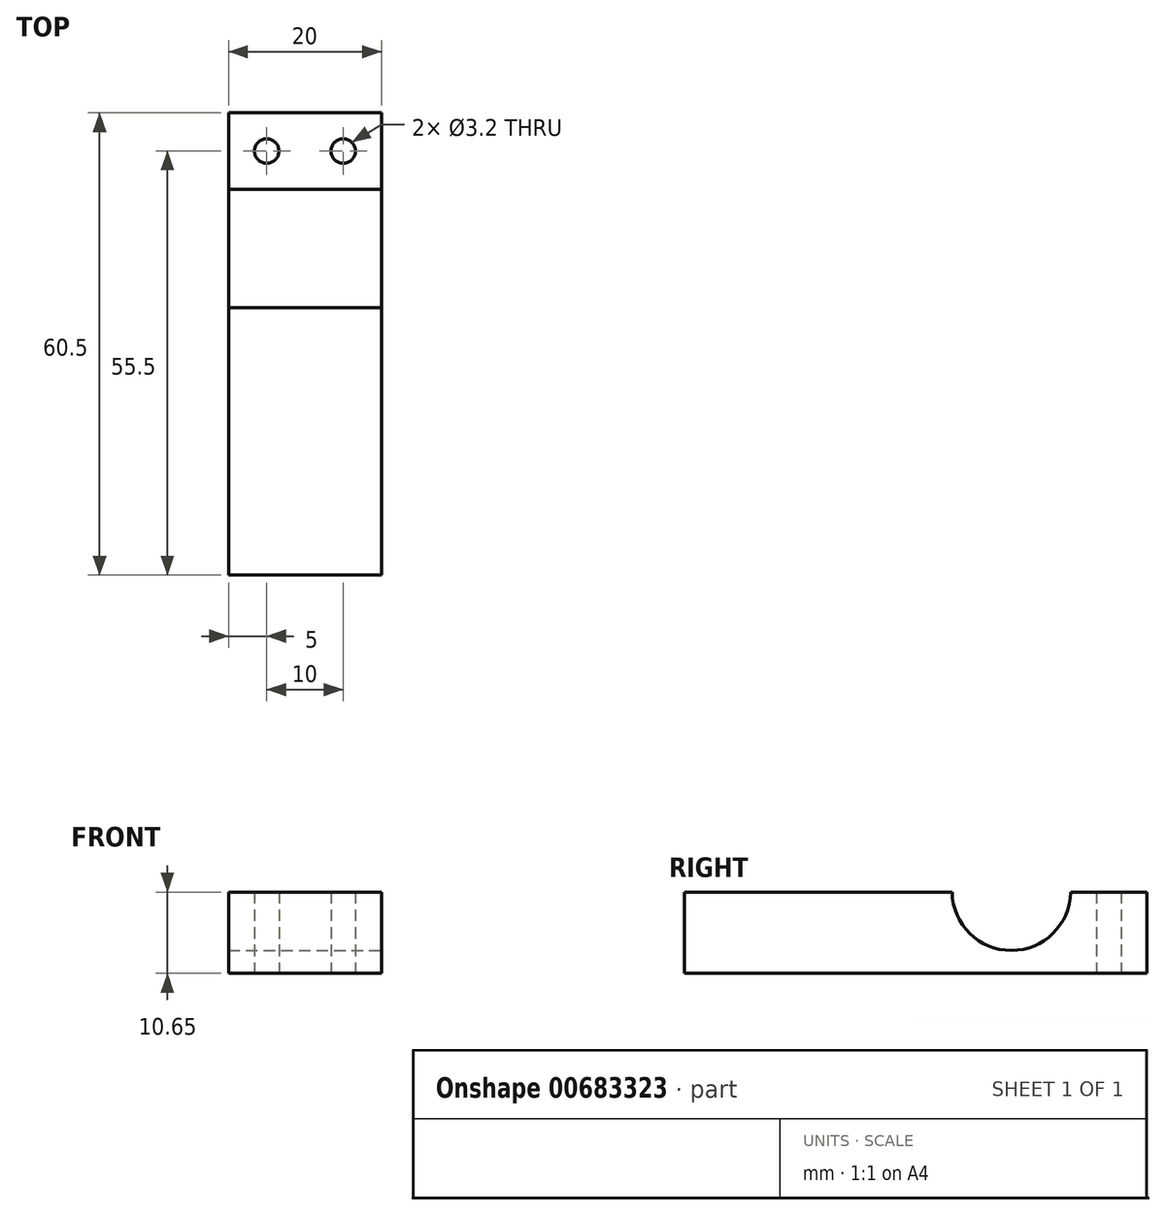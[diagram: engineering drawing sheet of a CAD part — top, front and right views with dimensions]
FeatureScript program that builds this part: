
annotation { "Feature Type Name" : "Feature", "Feature Type Description" : "" }
export const myFeature = defineFeature(function(context is Context, id is Id, definition is map)
    precondition{}
    {
        {
            var Q0;
            Q0=qCreatedBy(makeId("Top.planeOp"),FACE);
            var sketch = newSketch(context, id + "F0", { "sketchPlane" : qUnion([Q0])});
            skLineSegment(sketch, "E0.bottom", {"start": v(10, 15) * mm, "end": v(-10, 15) * mm});
            skLineSegment(sketch, "E0.top", {"start": v(10, -15) * mm, "end": v(-10, -15) * mm});
            skLineSegment(sketch, "E0.left", {"start": v(10, 15) * mm, "end": v(10, -15) * mm});
            skLineSegment(sketch, "E0.right", {"start": v(-10, 15) * mm, "end": v(-10, -15) * mm});
            skPoint(sketch, "E0.middle", {"position": v(0, 0) * mm});
            skLineSegment(sketch, "E1.bottom", {"start": v(-10, 15) * mm, "end": v(10, 15) * mm});
            skLineSegment(sketch, "E1.top", {"start": v(-10, 20) * mm, "end": v(10, 20) * mm});
            skLineSegment(sketch, "E1.left", {"start": v(-10, 15) * mm, "end": v(-10, 20) * mm});
            skLineSegment(sketch, "E1.right", {"start": v(10, 15) * mm, "end": v(10, 20) * mm});
            skLineSegment(sketch, "E2.top", {"start": v(-10, 35.5) * mm, "end": v(10, 35.5) * mm});
            skLineSegment(sketch, "E2.left", {"start": v(-10, 20) * mm, "end": v(-10, 35.5) * mm});
            skLineSegment(sketch, "E2.right", {"start": v(10, 20) * mm, "end": v(10, 35.5) * mm});
            skLineSegment(sketch, "E3.top", {"start": v(-10, 45.5) * mm, "end": v(10, 45.5) * mm});
            skLineSegment(sketch, "E3.left", {"start": v(-10, 35.5) * mm, "end": v(-10, 45.5) * mm});
            skLineSegment(sketch, "E3.right", {"start": v(10, 35.5) * mm, "end": v(10, 45.5) * mm});
            skLineSegment(sketch, "E4", {"start": v(0, 45.5) * mm, "end": v(0, 35.5) * mm, "construction": true});
            skLineSegment(sketch, "E5", {"start": v(0, 35.5) * mm, "end": v(10, 35.5) * mm});
            skLineSegment(sketch, "E6", {"start": v(5, 35.5) * mm, "end": v(5, 45.5) * mm, "construction": true});
            skLineSegment(sketch, "E7", {"start": v(0, 45.5) * mm, "end": v(-10, 45.5) * mm});
            skLineSegment(sketch, "E8", {"start": v(-5, 45.5) * mm, "end": v(-5, 35.5) * mm, "construction": true});
            skCircle(sketch, "E9", {"center": v(-5, 40.5) * mm, "radius": 1.6 * mm});
            skCircle(sketch, "E10", {"center": v(5, 40.5) * mm, "radius": 1.6 * mm});
            skSolve(sketch);
        }
        {
            var Q0;
            Q0 = qSketchRegion(id + "F0", true);
            extrude(context, id + "F1", {"entities" : qUnion([Q0]), "depth" : (15.5 / 2 + 3) * mm, "offsetDistance" : 25 * mm});
        }
        {
            var Q0;
            Q0=makeQuery(id+"F1.opExtrude","SWEPT_FACE",FACE,{"disambiguationData":[OSD([sQuery(id+"F0.wireOp",EDGE,"E0.left"),sQuery(id+"F0.wireOp",EDGE,"E1.right"),sQuery(id+"F0.wireOp",EDGE,"E2.right"),sQuery(id+"F0.wireOp",EDGE,"E3.right")])]});
            var sketch = newSketch(context, id + "F2", { "sketchPlane" : qUnion([Q0])});
            skLineSegment(sketch, "E11", {"start": v(45.5, 10.75) * mm, "end": v(35.5, 10.75) * mm});
            skLineSegment(sketch, "E12", {"start": v(35.5, 10.75) * mm, "end": v(20, 10.75) * mm});
            skCircle(sketch, "E13", {"center": v(27.75, 10.75) * mm, "radius": 7.75 * mm});
            skSolve(sketch);
        }
        {
            var Q0;
            Q0 = qSketchRegion(id + "F2", true);
            extrude(context, id + "F3", {"entities" : qUnion([Q0]), "operationType" : NewBodyOperationType.REMOVE, "oppositeDirection" : true, "depth" : 25 * mm, "offsetDistance" : 25 * mm});
        }
        {
            var Q0;
            {var subQ0=sQuery(id+"F0.wireOp",EDGE,"E0.top");var subQ1=sQuery(id+"F0.wireOp",EDGE,"E3.right");var subQ2=sQuery(id+"F0.wireOp",EDGE,"E2.right");var subQ3=sQuery(id+"F0.wireOp",EDGE,"E1.right");var subQ4=sQuery(id+"F0.wireOp",EDGE,"E0.left");var subQ5=sQuery(id+"F0.wireOp",EDGE,"E3.left");var subQ6=sQuery(id+"F0.wireOp",EDGE,"E2.left");var subQ7=sQuery(id+"F0.wireOp",EDGE,"E1.left");var subQ8=sQuery(id+"F0.wireOp",EDGE,"E0.right");Q0=makeQuery(id+"F3.boolean.opBoolean","SPLIT",FACE,{"disambiguationData":[TD([makeQuery(id+"F1.opExtrude","SWEPT_FACE",FACE,{"disambiguationData":[OSD([subQ0])]})])],"derivedFrom":makeQuery(id+"F1.opExtrude","CAP_FACE",FACE,{"disambiguationData":[OSD([subQ0,subQ4,subQ8,subQ7,subQ3,subQ6,subQ2,sQuery(id+"F0.wireOp",EDGE,"E3.top"),subQ5,subQ1,sQuery(id+"F0.wireOp",EDGE,"E7"),sQuery(id+"F0.wireOp",EDGE,"E9"),sQuery(id+"F0.wireOp",EDGE,"E10")])],"isStart":false})});}
            var sketch = newSketch(context, id + "F4", { "sketchPlane" : qUnion([Q0])});
            skLineSegment(sketch, "E14.bottom", {"start": v(-15.06, -24.53) * mm, "end": v(22.55, -24.53) * mm});
            skLineSegment(sketch, "E14.top", {"start": v(-15.06, 68.7) * mm, "end": v(22.55, 68.7) * mm});
            skLineSegment(sketch, "E14.left", {"start": v(-15.06, -24.53) * mm, "end": v(-15.06, 68.7) * mm});
            skLineSegment(sketch, "E14.right", {"start": v(22.55, -24.53) * mm, "end": v(22.55, 68.7) * mm});
            skSolve(sketch);
        }
        {
            var Q0;
            Q0 = qSketchRegion(id + "F4", true);
            extrude(context, id + "F5", {"entities" : qUnion([Q0]), "operationType" : NewBodyOperationType.REMOVE, "oppositeDirection" : true, "depth" : 0.1 * mm, "offsetDistance" : 25 * mm});
        }
    });
